# Revit family: 1HVAC_Ductwork_Airzone_Return-Grille_RRLG
name_source: partatom
category: Air Terminals
revit_build: Autodesk Revit 2016 (Build: 20161004_0715(x64)
units: mm (PartAtom-declared; Revit-internal decimal feet)

## family parameters
Always vertical = Yes
Cut with Voids When Loaded = No
OmniClass Number = 23.75.70.21.27.11
OmniClass Title = Diffusers, Registers, and Grilles
Part Type = Normal
Room Calculation Point = Yes
Round Connector Dimension = Use Diameter
Shared = No
Work Plane-Based = No

## types (1)
- INVALID TYPE - Use Load Family and Type Catalog instead
    Accessories Material = Metal - AIRZONE - Extruded Aluminium - Anodized (Matt Silver Color)
    Ak = 0.44
    Compatible Accesories = Mounting frame. Plenum for grille (PREJ). Antiparticle filter (FILT).
    Description = Fixed wide-slat return grille
    Disclaimer = All information provided in this model is reviewed before being published. However, Airzone cannot guarantee this model is error-free, therefore users are strongly encouraged to check for technical documentation and updates
    Duct Height = 150 mm
    Duct Width = 300 mm
    Effective Area = 44.00 cm²
    Finish = White (RAL 9010)
    Fixing = Clip (K), mounting frame required. Screw (T), mounting frame required.
    Grille Material = Metal - AIRZONE - Grille 25 mm - White (RAL 9010)
    Long Description = Extruded aluminum supply grille with anti-vision horizontal slats that do not let elements pass through and enable the air flow. 26-mm standard frame.
    Main Material = Metal - AIRZONE - Extruded Aluminium - White (RAL 9010)
    Manufacturer = AIRZONE
    Max Flow = 2000 m³/h
    Min Flow = 50 m³/h
    Model = INVALID – Type not loaded via type catalog
    Product Code = INVALID – Type not loaded via type catalog
    Product Comments = Refer to technical documentation for further details
    Product Documentation Download URL = http://doc.airzone.es
    Revit Model Version = 1.0
    Type Image Comments = Image available in product documentation download
    URL = www.airzone.es
    c1 = 0.001198
    c2 = -1.999
    c3 = -85.8
    c4 = -49.09
    c5 = 57.03
    c6 = 0
    c7 = 0
    c8 = 0

## geometry (parser evidence)
native form markers: Sweep x2
no freeform markers — native parametric forms only
